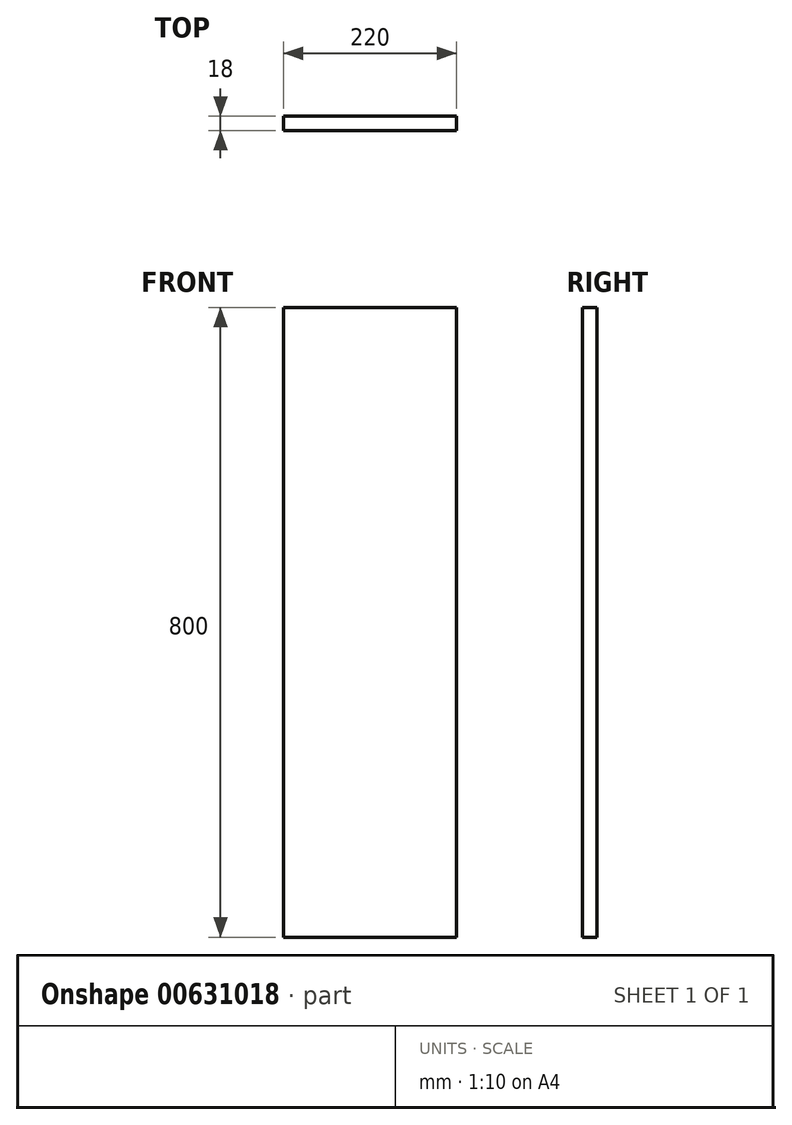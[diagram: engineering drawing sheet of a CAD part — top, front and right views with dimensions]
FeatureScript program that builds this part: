
annotation { "Feature Type Name" : "Feature", "Feature Type Description" : "" }
export const myFeature = defineFeature(function(context is Context, id is Id, definition is map)
    precondition{}
    {
        {
            var Q0;
            Q0=qCreatedBy(makeId("Front.planeOp"),FACE);
            var sketch = newSketch(context, id + "F0", { "sketchPlane" : qUnion([Q0])});
            skLineSegment(sketch, "E0.bottom", {"start": v(0, 0) * mm, "end": v(-220, 0) * mm});
            skLineSegment(sketch, "E0.top", {"start": v(0, -800) * mm, "end": v(-220, -800) * mm});
            skLineSegment(sketch, "E0.left", {"start": v(0, 0) * mm, "end": v(0, -800) * mm});
            skLineSegment(sketch, "E0.right", {"start": v(-220, 0) * mm, "end": v(-220, -800) * mm});
            skSolve(sketch);
        }
        {
            var Q0;
            Q0 = qSketchRegion(id + "F0", true);
            extrude(context, id + "F1", {"entities" : qUnion([Q0]), "depth" : 18 * mm, "offsetDistance" : 25 * mm});
        }
    });
